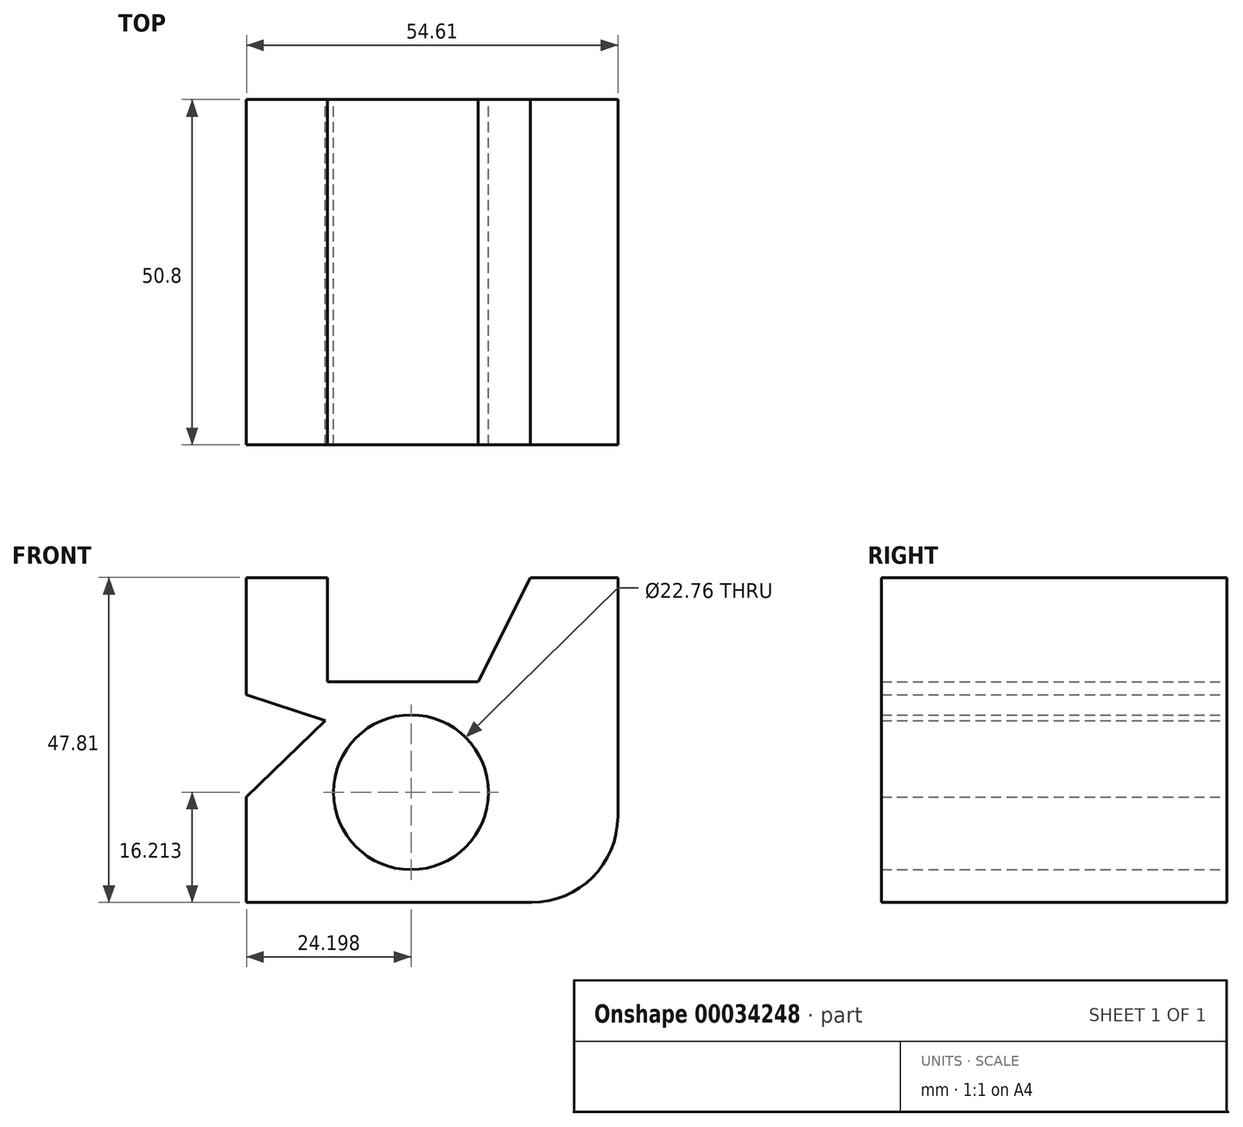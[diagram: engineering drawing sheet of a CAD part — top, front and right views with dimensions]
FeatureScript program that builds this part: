
annotation { "Feature Type Name" : "Feature", "Feature Type Description" : "" }
export const myFeature = defineFeature(function(context is Context, id is Id, definition is map)
    precondition{}
    {
        {
            var Q0;
            Q0=qCreatedBy(makeId("Front.planeOp"),FACE);
            var sketch = newSketch(context, id + "F0", { "sketchPlane" : qUnion([Q0])});
            skLineSegment(sketch, "E0.bottom", {"start": v(-54.61, 26.22) * mm, "end": v(-42.69, 26.22) * mm});
            skLineSegment(sketch, "E0.top", {"start": v(-54.61, -21.6) * mm, "end": v(-12.7, -21.6) * mm});
            skLineSegment(sketch, "E0.left", {"start": v(-54.61, 26.22) * mm, "end": v(-54.61, 9) * mm});
            skLineSegment(sketch, "E0.right", {"start": v(0, 26.22) * mm, "end": v(0, -8.9) * mm});
            skLineSegment(sketch, "E1", {"start": v(-42.69, 26.22) * mm, "end": v(-42.69, 10.91) * mm});
            skLineSegment(sketch, "E2", {"start": v(-42.69, 10.91) * mm, "end": v(-20.54, 10.91) * mm});
            skLineSegment(sketch, "E3", {"start": v(-20.54, 10.91) * mm, "end": v(-12.83, 26.22) * mm});
            skLineSegment(sketch, "E4.trimOffspring", {"start": v(-12.83, 26.22) * mm, "end": v(0, 26.22) * mm});
            skPoint(sketch, "E5.visualSharp", {"position": v(0, -21.6) * mm});
            skArc(sketch, "E5.filletArc", {"start": v(-12.7, -21.6) * mm, "mid": v(-3.72, -17.87) * mm, "end": v(0, -8.9) * mm});
            skCircle(sketch, "E6", {"center": v(-30.41, -5.38) * mm, "radius": 11.38 * mm});
            skLineSegment(sketch, "E7", {"start": v(-54.61, 9) * mm, "end": v(-43.04, 5.18) * mm});
            skLineSegment(sketch, "E8", {"start": v(-43.04, 5.18) * mm, "end": v(-54.61, -6.06) * mm});
            skLineSegment(sketch, "E9.trimOffspring", {"start": v(-54.61, -6.06) * mm, "end": v(-54.61, -21.6) * mm});
            skSolve(sketch);
        }
        {
            var Q0;
            Q0 = qSketchRegion(id + "F0", true);
            extrude(context, id + "F1", {"entities" : qUnion([Q0]), "depth" : 50.8 * mm});
        }
    });
